# Revit family: v-241bk5-rn_60Hz
name_source: partatom
category: 機械設備
units: mm (PartAtom-declared; Revit-internal decimal feet)

## family parameters
OmniClass タイトル = Centrifugal Fans
OmniClass 番号 = 23.75.35.17.27
パーツ タイプ = 標準
ロード時にボイドで切り取り = いいえ
丸型コネクタ寸法 = 直径を使用
作業面ベース = いいえ
共有 = いいえ
常に垂直 = はい
部屋計算ポイント = いいえ

## types (1)
- V-241BK5-RN
    Clearance Back = 0  [stored 0 ft]
    Clearance Bottom = 100  [stored 0.328084 ft]
    Clearance Front = 100  [stored 0.328084 ft]
    Clearance Left = 100  [stored 0.328084 ft]
    Clearance Right = 100  [stored 0.328084 ft]
    Clearance Top = 100  [stored 0.328084 ft]
    D1 = 135  [stored 0.442913 ft]
    Depth = 175  [stored 0.574147 ft]
    H1 = 106  [stored 0.347769 ft]
    Height = 280
    IfcExportAs = IfcFanType
    IfcExportType = PROPELLORAXIAL
    MAX静圧 = 0.0 Pa
    MAX風量 = 195.0 m³/h
    MID静圧 = 0.0 Pa
    MID風量 = 195.0 m³/h
    MIN静圧 = 0.0 Pa
    MIN風量 = 100.0 m³/h
    OmniClassCode = 23-33 31 19 11 15
    URL = https://www.mitsubishielectric.co.jp
    Uniclass2015Code = Pr_65_67_29_12
    Uniclass2015Title = Centrifugal fans
    Uniclass2015Version = Systems v1.9
    W1 = 122  [stored 0.400262 ft]
    Width = 498  [stored 1.63386 ft]
    マテリアル = 合成樹脂(白)
    メンテナンススペース = はい
    モデル = V-241BK5-RN
    仕様書バージョン = Version1.0
    企業コード = 108420
    価格 = 166500 $
    分類コード = 50052503100080
    周波数 = 60 Hz
    極数 = 3
    法定耐用年数 = 10
    消費電力 = 2190 W
    相 = 1
    積算_科目 = 2 換気設備
    製品リリース年月 = 2022年6月1日
    製品出荷対象 = 国内
    製品質量 = 9.00 kg
    製造元 = 三菱電機株式会社
    設置方法 = 壁付
    説明 = バス乾燥・暖房・換気システム リニューアルバスカラット
    負荷分類 = 3_ファン類
    質量 = 10.80 kg
    運転質量 = 0.00 kg
    電動機出力 = 0 W
    電圧 = 200 V

note: [stored X ft] marks values corroborated as IEEE doubles in the binary element streams (Revit-internal decimal feet)
